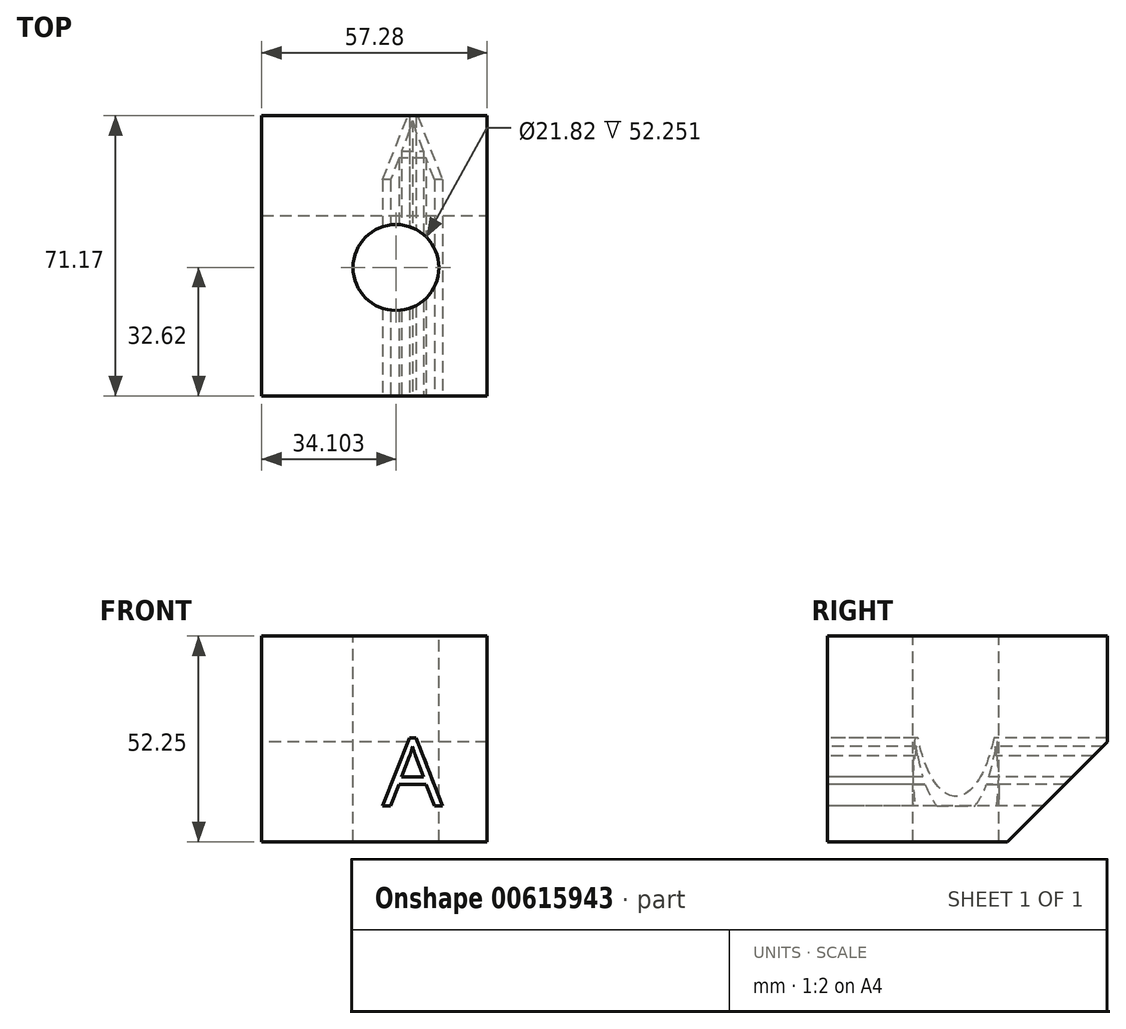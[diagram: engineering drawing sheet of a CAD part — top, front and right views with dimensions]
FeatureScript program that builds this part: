
annotation { "Feature Type Name" : "Feature", "Feature Type Description" : "" }
export const myFeature = defineFeature(function(context is Context, id is Id, definition is map)
    precondition{}
    {
        {
            var Q0;
            Q0=qCreatedBy(makeId("Top.planeOp"),FACE);
            var sketch = newSketch(context, id + "F0", { "sketchPlane" : qUnion([Q0])});
            skLineSegment(sketch, "E0.bottom", {"start": v(9.78, 38.55) * mm, "end": v(-47.5, 38.55) * mm});
            skLineSegment(sketch, "E0.top", {"start": v(9.78, -32.62) * mm, "end": v(-47.5, -32.62) * mm});
            skLineSegment(sketch, "E0.left", {"start": v(9.78, 38.55) * mm, "end": v(9.78, -32.62) * mm});
            skLineSegment(sketch, "E0.right", {"start": v(-47.5, 38.55) * mm, "end": v(-47.5, -32.62) * mm});
            skSolve(sketch);
        }
        {
            var Q0;
            Q0 = qSketchRegion(id + "F0", true);
            extrude(context, id + "F1", {"entities" : qUnion([Q0]), "depth" : 52.25 * mm, "offsetDistance" : 25.4 * mm});
        }
        {
            var Q0;
            Q0=makeQuery(id+"F1.opExtrude","CAP_FACE",FACE,{"disambiguationData":[OSD([sQuery(id+"F0.wireOp",EDGE,"E0.bottom"),sQuery(id+"F0.wireOp",EDGE,"E0.top"),sQuery(id+"F0.wireOp",EDGE,"E0.left"),sQuery(id+"F0.wireOp",EDGE,"E0.right")])],"isStart":false});
            var sketch = newSketch(context, id + "F2", { "sketchPlane" : qUnion([Q0])});
            skCircle(sketch, "E1", {"center": v(-13.4, 0) * mm, "radius": 10.9 * mm});
            skSolve(sketch);
        }
        {
            var Q0;
            Q0=makeQuery(id+"F2.imprint","IMPRINT",FACE,{"disambiguationData":[TD([[makeQuery(id+"F2.imprint","IMPRINT",EDGE,{"derivedFrom":sQuery(id+"F2.wireOp",EDGE,"E1")}),1.0]])]});
            extrude(context, id + "F3", {"entities" : qUnion([Q0]), "operationType" : NewBodyOperationType.REMOVE, "oppositeDirection" : true, "depth" : 374.23 * mm, "offsetDistance" : 25.4 * mm});
        }
        {
            var Q0;
            Q0=makeQuery(id+"F1.opExtrude","CAP_EDGE",EDGE,{"disambiguationData":[OSD([sQuery(id+"F0.wireOp",EDGE,"E0.bottom")])],"isStart":true});
            chamfer(context, id + "F4", {"entities" : qUnion([Q0]), "width" : 25.4 * mm, "tangentPropagation" : true});
        }
        {
            var Q0;
            Q0=makeQuery(id+"F1.opExtrude","SWEPT_FACE",FACE,{"disambiguationData":[OSD([sQuery(id+"F0.wireOp",EDGE,"E0.top")])]});
            var sketch = newSketch(context, id + "F5", { "sketchPlane" : qUnion([Q0])});
            skText(sketch, "E2", { "text": "A", "fontName": "OpenSans-Regular.ttf"});
            const initialGuessF5  = {"E2": [-0.0168, 0.00914, 1, 0, 0.01734]};
            skSetInitialGuess(sketch, initialGuessF5);
            skSolve(sketch);
        }
        {
            var Q0;
            Q0 = qSketchRegion(id + "F5", true);
            extrude(context, id + "F6", {"entities" : qUnion([Q0]), "operationType" : NewBodyOperationType.REMOVE, "oppositeDirection" : true, "depth" : 171.07 * mm, "offsetDistance" : 25.4 * mm});
        }
    });
